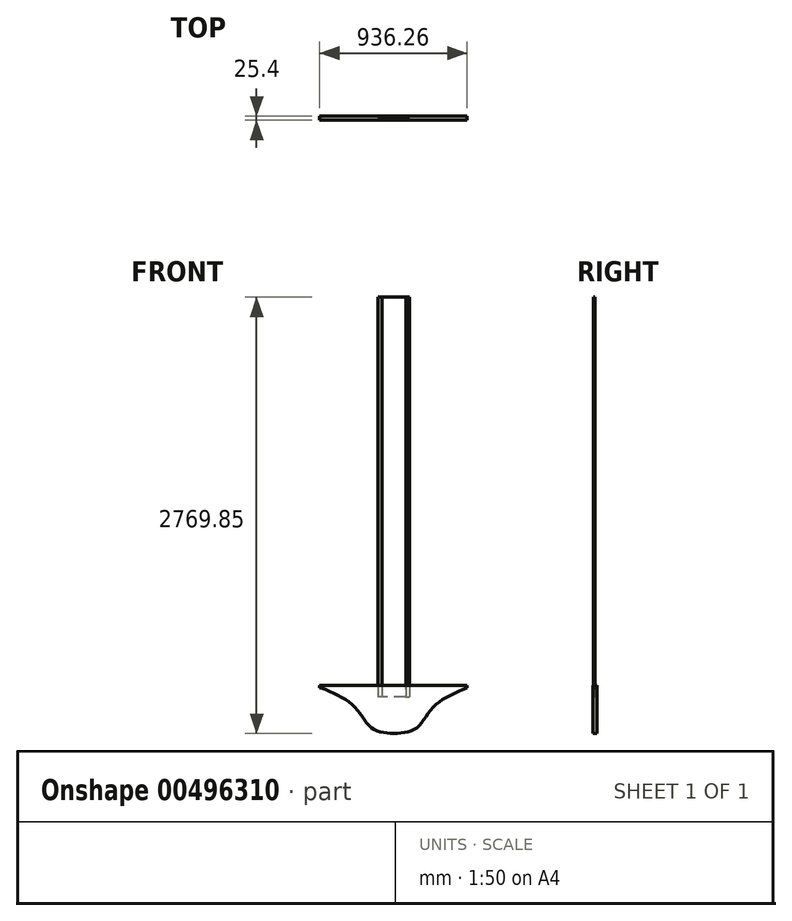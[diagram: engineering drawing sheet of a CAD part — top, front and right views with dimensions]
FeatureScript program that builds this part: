
annotation { "Feature Type Name" : "Feature", "Feature Type Description" : "" }
export const myFeature = defineFeature(function(context is Context, id is Id, definition is map)
    precondition{}
    {
        {
            var Q0;
            Q0=qCreatedBy(makeId("Top.planeOp"),FACE);
            var sketch = newSketch(context, id + "F0", { "sketchPlane" : qUnion([Q0])});
            skLineSegment(sketch, "E0.left", {"start": v(-77.78, -0.01) * mm, "end": v(-77.78, -3.48) * mm});
            skLineSegment(sketch, "E0.right", {"start": v(74.2, -0.01) * mm, "end": v(74.2, -3.48) * mm});
            skLineSegment(sketch, "E1.bottom", {"start": v(-77.78, -3.48) * mm, "end": v(-103.4, -3.48) * mm});
            skLineSegment(sketch, "E1.top", {"start": v(-77.78, -0.01) * mm, "end": v(-103.4, -0.01) * mm});
            skLineSegment(sketch, "E1.left", {"start": v(-77.78, -3.48) * mm, "end": v(-77.78, -0.01) * mm});
            skLineSegment(sketch, "E1.right", {"start": v(-103.4, -3.48) * mm, "end": v(-103.4, -0.01) * mm});
            skLineSegment(sketch, "E2.bottom", {"start": v(74.2, -3.48) * mm, "end": v(99.66, -3.48) * mm});
            skLineSegment(sketch, "E2.top", {"start": v(74.2, -0.01) * mm, "end": v(99.66, -0.01) * mm});
            skLineSegment(sketch, "E2.left", {"start": v(74.2, -3.48) * mm, "end": v(74.2, -0.01) * mm});
            skLineSegment(sketch, "E2.right", {"start": v(99.66, -3.48) * mm, "end": v(99.66, -0.01) * mm});
            skLineSegment(sketch, "E3.bottom", {"start": v(74.2, -0.01) * mm, "end": v(-77.78, -0.01) * mm});
            skLineSegment(sketch, "E3.top", {"start": v(74.2, -10.93) * mm, "end": v(-77.78, -10.93) * mm});
            skLineSegment(sketch, "E3.left", {"start": v(74.2, -0.01) * mm, "end": v(74.2, -10.93) * mm});
            skLineSegment(sketch, "E3.right", {"start": v(-77.78, -0.01) * mm, "end": v(-77.78, -10.93) * mm});
            skSolve(sketch);
        }
        {
            var Q0;
            {var subQ3=sQuery(id+"F0.wireOp",EDGE,"E3.bottom");Q0=makeQuery(id+"F0.imprint","IMPRINT",FACE,{"disambiguationData":[TD([[makeQuery(id+"F0.imprint","IMPRINT",EDGE,{"derivedFrom":subQ3}),1.0]])]});}
            extrude(context, id + "F1", {"entities" : qUnion([Q0]), "depth" : 2540 * mm});
        }
        {
            var Q0;
            Q0=qCreatedBy(makeId("Front.planeOp"),FACE);
            var sketch = newSketch(context, id + "F2", { "sketchPlane" : qUnion([Q0])});
            skLineSegment(sketch, "E4.bottom", {"start": v(463.59, 58.96) * mm, "end": v(-472.67, 58.96) * mm});
            skLineSegment(sketch, "E4.top", {"start": v(463.59, 75.33) * mm, "end": v(-472.67, 75.33) * mm});
            skLineSegment(sketch, "E4.left", {"start": v(463.59, 74.71) * mm, "end": v(463.59, 75.33) * mm});
            skLineSegment(sketch, "E4.right", {"start": v(-472.67, 58.96) * mm, "end": v(-472.67, 75.33) * mm});
            skLineSegment(sketch, "E5", {"start": v(463.59, 75.33) * mm, "end": v(463.59, 58.96) * mm});
            skFitSpline(sketch, "E6", {"points": [v(463.59, 58.96) * mm, v(252.06, -60.05) * mm, v(140.07, -197.34) * mm, v(0, -229.85) * mm], "startDerivative": vector(-625.74, -257.44) * mm, "endDerivative": vector(-523.48, -26.1) * mm});
            skFitSpline(sketch, "E7.MirrorCS", {"points": [v(-463.59, 58.96) * mm, v(-252.06, -60.05) * mm, v(-140.07, -197.34) * mm, v(0, -229.85) * mm], "startDerivative": vector(625.74, -257.44) * mm, "endDerivative": vector(523.48, -26.1) * mm});
            skSolve(sketch);
        }
        {
            var Q0;
            Q0 = qSketchRegion(id + "F2", true);
            extrude(context, id + "F3", {"entities" : qUnion([Q0]), "endBound" : BoundingType.SYMMETRIC, "depth" : 25.4 * mm});
        }
        {
            var Q0;
            Q0=qCreatedBy(makeId("Top.planeOp"),FACE);
            var sketch = newSketch(context, id + "F4", { "sketchPlane" : qUnion([Q0])});
            skLineSegment(sketch, "E8.bottom", {"start": v(73.23, -9.44) * mm, "end": v(98.9, -9.44) * mm});
            skLineSegment(sketch, "E8.top", {"start": v(73.23, -5.63) * mm, "end": v(98.9, -5.63) * mm});
            skLineSegment(sketch, "E8.left", {"start": v(73.23, -9.44) * mm, "end": v(73.23, -5.63) * mm});
            skLineSegment(sketch, "E8.right", {"start": v(98.9, -9.44) * mm, "end": v(98.9, -5.63) * mm});
            skPoint(sketch, "E9.oppositeSnap0", {"position": v(86.06, -5.63) * mm});
            skLineSegment(sketch, "E9.bottom", {"start": v(-76.25, -9.7) * mm, "end": v(-101.92, -9.7) * mm});
            skLineSegment(sketch, "E9.top", {"start": v(-76.25, -5.63) * mm, "end": v(-101.92, -5.63) * mm});
            skLineSegment(sketch, "E9.left", {"start": v(-76.25, -9.7) * mm, "end": v(-76.25, -5.63) * mm});
            skLineSegment(sketch, "E9.right", {"start": v(-101.92, -9.7) * mm, "end": v(-101.92, -5.63) * mm});
            skSolve(sketch);
        }
        {
            var Q0;
            Q0=makeQuery(id+"F4.imprint","IMPRINT",FACE,{"disambiguationData":[TD([[makeQuery(id+"F4.imprint","IMPRINT",EDGE,{"derivedFrom":sQuery(id+"F4.wireOp",EDGE,"E9.bottom")}),-1.0]])]});
            var Q1;
            Q1=makeQuery(id+"F4.imprint","IMPRINT",FACE,{"disambiguationData":[TD([[makeQuery(id+"F4.imprint","IMPRINT",EDGE,{"derivedFrom":sQuery(id+"F4.wireOp",EDGE,"E8.bottom")}),1.0]])]});
            extrude(context, id + "F5", {"entities" : qUnion([Q0, Q1]), "depth" : 2540 * mm});
        }
    });
